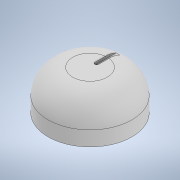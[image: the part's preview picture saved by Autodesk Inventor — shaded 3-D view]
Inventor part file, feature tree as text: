
AUTODESK INVENTOR PART (.ipt)
format: ipt  version: 2022 (Build 260153000, 153)  size: 207,360 bytes
history: native  units: in
note: dims shown in document units (in); Inventor stores cm internally (conversion verified against a paired STEP export)
features: extrude x4, sketch x4, chamfer x2, fillet x2
ambient origin geometry x8: Origin, YZ Plane, XZ Plane, XY Plane, X Axis, Y Axis, Z Axis, Center Point
bodies: Solid1 (feature_tree)
feature tree (12):
  extrude  "Extrusion1"  Depth=0.5118in TaperAngle=0.0deg
  chamfer  "Chamfer1"  Distance=0.1575in Angle=45.0deg
  extrude  "Extrusion2"  Depth=0.3937in
  fillet  "Fillet1"  Radius=0.0787in
  extrude  "Extrusion7"  Depth=0.0394in TaperAngle=0.0deg
  extrude  "Extrusion8"  Depth=0.3937in
  chamfer  "Chamfer2"  Distance=0.4134in
  fillet  "Fillet6"  Radius=0.1181in
  sketch  "Sketch1"  dims[d0=1.3386in d1=0.5118in d2=0.0in d3=0.1575in d4=0.0787in d5=45.0deg]
  sketch  "Sketch2"  dims[d6=0.0591in d7=0.3937in d8=0.0787in]
  sketch  "Sketch3"  dims[d9=0.6398in d10=0.0394in d11=0.0in]
  sketch  "Sketch5"  dims[d12=0.0295in d13=0.2283in d41=0.4134in d42=0.0in d45=0.1181in d46=0.0in d50=0.6843in d52=0.6843in d54=0.8589in d55=0.8589in d57=0.0197in d58=0.0787in d59=45.0deg d63=0.3937in d35=0.0197in d36=0.0344in d37=0.0197in d38=0.0344in d61=0.0in d62=0.0in d64=0.0in]
